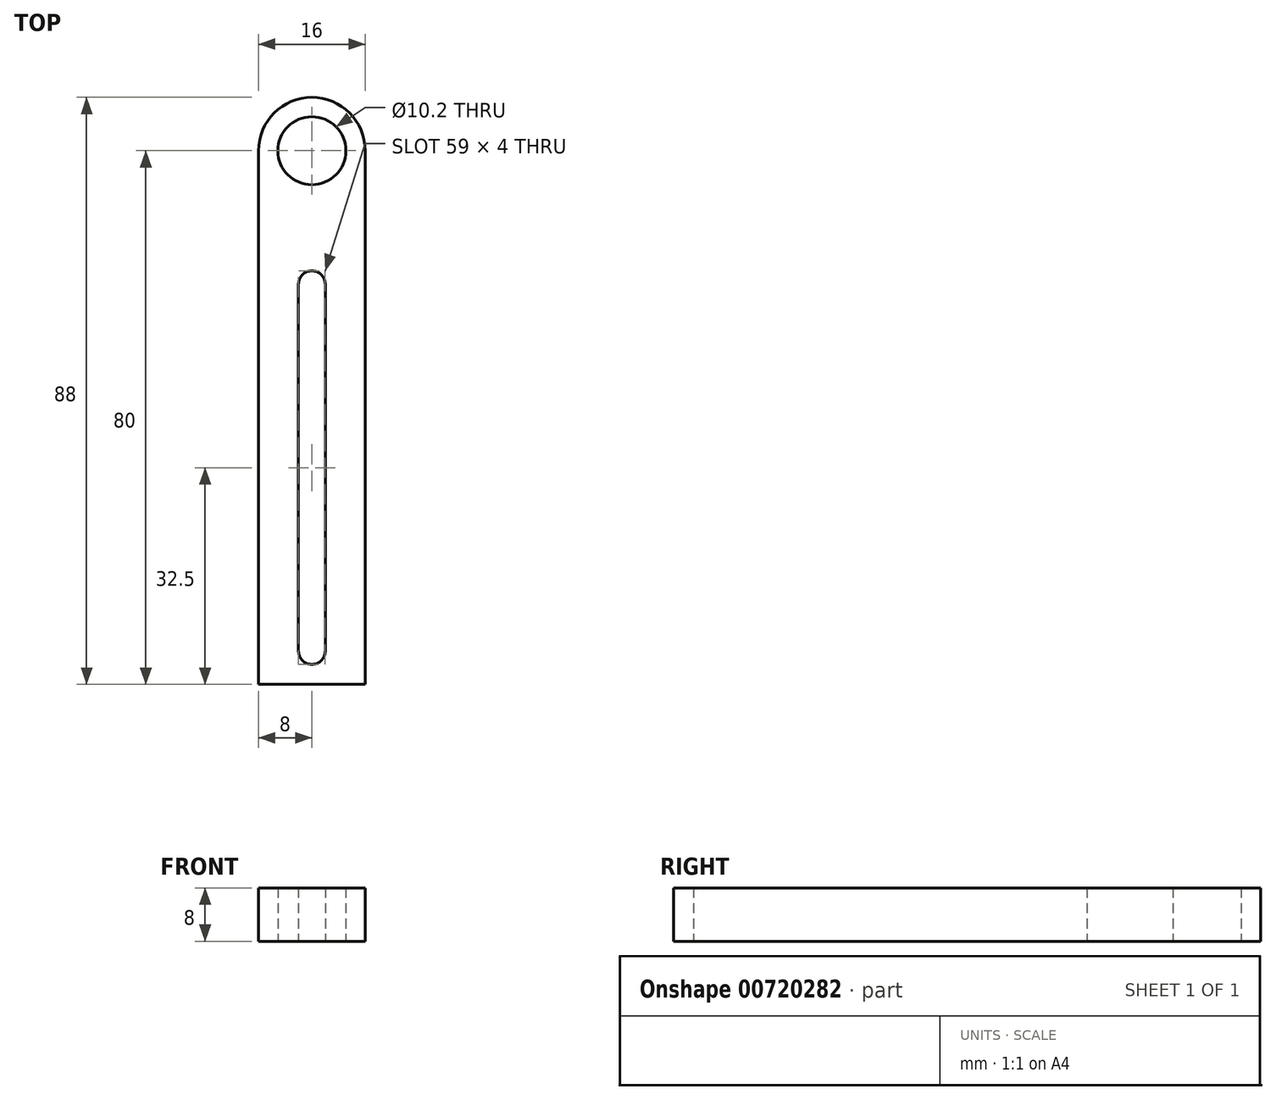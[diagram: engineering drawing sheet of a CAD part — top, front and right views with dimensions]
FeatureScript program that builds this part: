
annotation { "Feature Type Name" : "Feature", "Feature Type Description" : "" }
export const myFeature = defineFeature(function(context is Context, id is Id, definition is map)
    precondition{}
    {
        {
            var Q0;
            Q0=qCreatedBy(makeId("Top.planeOp"),FACE);
            var sketch = newSketch(context, id + "F0", { "sketchPlane" : qUnion([Q0])});
            skCircle(sketch, "E0", {"center": v(0, 0) * mm, "radius": 5.1 * mm});
            skCircle(sketch, "E1", {"center": v(0, 0) * mm, "radius": 8 * mm});
            skLineSegment(sketch, "E2.bottom", {"start": v(-8, 0) * mm, "end": v(8, 0) * mm});
            skLineSegment(sketch, "E2.top", {"start": v(-8, -80) * mm, "end": v(8, -80) * mm});
            skLineSegment(sketch, "E2.left", {"start": v(-8, 0) * mm, "end": v(-8, -80) * mm});
            skLineSegment(sketch, "E2.right", {"start": v(8, 0) * mm, "end": v(8, -80) * mm});
            skCircle(sketch, "E3", {"center": v(0, -20) * mm, "radius": 2 * mm});
            skCircle(sketch, "E4", {"center": v(0, -75) * mm, "radius": 2 * mm});
            skLineSegment(sketch, "E5.bottom", {"start": v(-2, -20) * mm, "end": v(2, -20) * mm});
            skLineSegment(sketch, "E5.top", {"start": v(-2, -75) * mm, "end": v(2, -75) * mm});
            skLineSegment(sketch, "E5.left", {"start": v(-2, -20) * mm, "end": v(-2, -75) * mm});
            skLineSegment(sketch, "E5.right", {"start": v(2, -20) * mm, "end": v(2, -75) * mm});
            skSolve(sketch);
        }
        {
            var Q0;
            {var subQ0=sQuery(id+"F0.wireOp",EDGE,"E2.bottom");var subQ1=sQuery(id+"F0.wireOp",EDGE,"E0");var subQ2=makeQuery(id+"F0.imprint","INTERSECT",VERTEX,{"disambiguationData":[OD(0.0)],"derivedFrom":[subQ1,subQ0]});Q0=makeQuery(id+"F0.imprint","IMPRINT",FACE,{"disambiguationData":[TD([[makeQuery(id+"F0.imprint","IMPRINT",EDGE,{"disambiguationData":[TD([[subQ2,-1.0]])],"derivedFrom":subQ1}),-1.0]])]});}
            var Q1;
            {var subQ0=sQuery(id+"F0.wireOp",EDGE,"E2.bottom");var subQ1=sQuery(id+"F0.wireOp",EDGE,"E0");var subQ2=makeQuery(id+"F0.imprint","INTERSECT",VERTEX,{"disambiguationData":[OD(0.0)],"derivedFrom":[subQ1,subQ0]});Q1=makeQuery(id+"F0.imprint","IMPRINT",FACE,{"disambiguationData":[TD([[makeQuery(id+"F0.imprint","IMPRINT",EDGE,{"disambiguationData":[TD([[subQ2,1.0]])],"derivedFrom":subQ1}),-1.0]])]});}
            var Q2;
            Q2=makeQuery(id+"F0.imprint","IMPRINT",FACE,{"disambiguationData":[TD([[makeQuery(id+"F0.imprint","IMPRINT",EDGE,{"derivedFrom":sQuery(id+"F0.wireOp",EDGE,"E2.top")}),1.0]])]});
            extrude(context, id + "F1", {"entities" : qUnion([Q0, Q1, Q2]), "depth" : 8 * mm, "offsetDistance" : 25 * mm});
        }
    });
